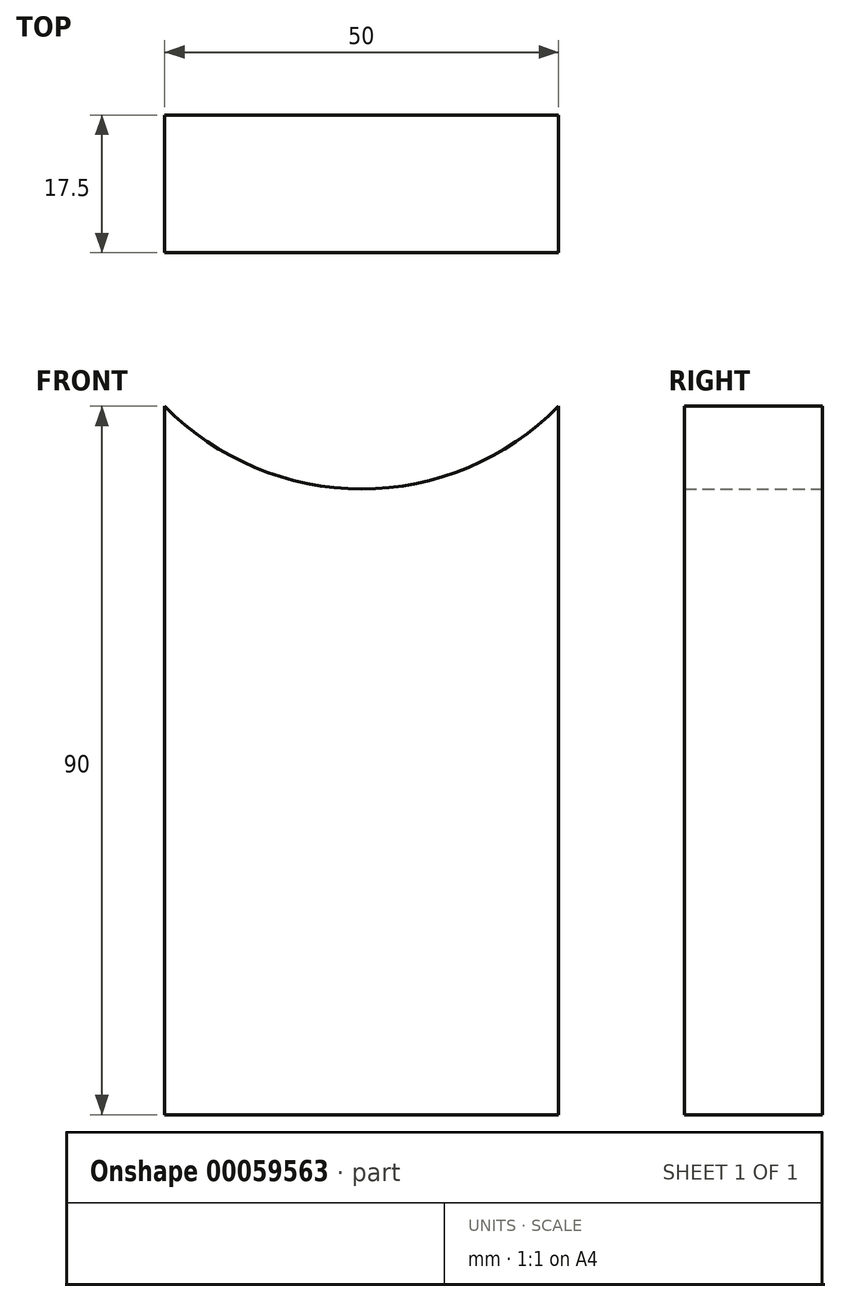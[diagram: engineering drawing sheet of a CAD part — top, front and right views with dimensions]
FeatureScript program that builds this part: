
annotation { "Feature Type Name" : "Feature", "Feature Type Description" : "" }
export const myFeature = defineFeature(function(context is Context, id is Id, definition is map)
    precondition{}
    {
        {
            var Q0;
            Q0=qCreatedBy(makeId("Front.planeOp"),FACE);
            var sketch = newSketch(context, id + "F0", { "sketchPlane" : qUnion([Q0])});
            skLineSegment(sketch, "E0.rect.top", {"start": v(-25, -45) * mm, "end": v(25, -45) * mm});
            skLineSegment(sketch, "E0.rect.left", {"start": v(-25, 45) * mm, "end": v(-25, -45) * mm});
            skLineSegment(sketch, "E0.rect.right", {"start": v(25, 45) * mm, "end": v(25, -45) * mm});
            skPoint(sketch, "E0.rect.middle", {"position": v(0, 0) * mm});
            skArc(sketch, "E1", {"start": v(-25, 45) * mm, "mid": v(0, 34.5) * mm, "end": v(25, 45) * mm});
            skSolve(sketch);
        }
        {
            var Q0;
            Q0=makeQuery(id+"F0.imprint","IMPRINT",FACE,{"disambiguationData":[TD([[makeQuery(id+"F0.imprint","IMPRINT",EDGE,{"derivedFrom":sQuery(id+"F0.wireOp",EDGE,"E0.rect.top")}),1.0]])]});
            extrude(context, id + "F1", {"entities" : qUnion([Q0]), "depth" : 17.5 * mm});
        }
    });
